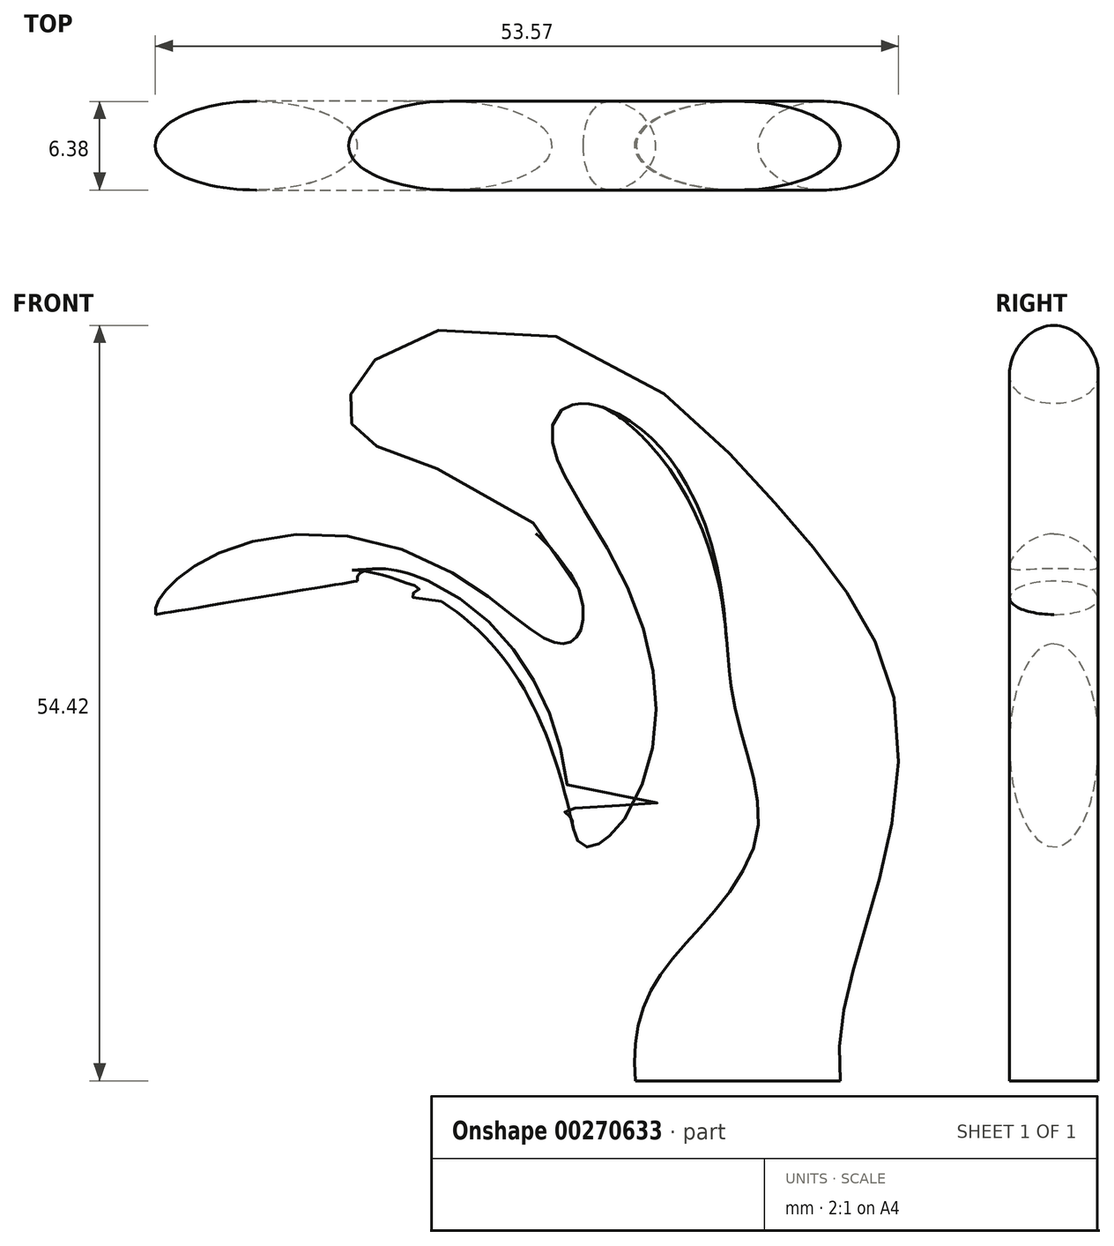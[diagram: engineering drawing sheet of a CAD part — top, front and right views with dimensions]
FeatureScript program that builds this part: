
annotation { "Feature Type Name" : "Feature", "Feature Type Description" : "" }
export const myFeature = defineFeature(function(context is Context, id is Id, definition is map)
    precondition{}
    {
        {
            var Q0;
            Q0=qCreatedBy(makeId("Top.planeOp"),FACE);
            var sketch = newSketch(context, id + "F0", { "sketchPlane" : qUnion([Q0])});
            skEllipse(sketch, "E0", {"center": v(0, 0) * mm, "majorRadius": 7.37 * mm, "minorRadius": 3.2 * mm, "majorAxis": v(1, 0)});
            skSolve(sketch);
        }
        {
            var Q0;
            Q0=qCreatedBy(makeId("Front.planeOp"),FACE);
            var sketch = newSketch(context, id + "F1", { "sketchPlane" : qUnion([Q0])});
            skLineSegment(sketch, "E1", {"start": v(0, 0) * mm, "end": v(0, 17.51) * mm});
            skFitSpline(sketch, "E2", {"points": [v(0, 17.51) * mm, v(-6, 33.73) * mm, v(-21.54, 36.47) * mm, v(-23.97, 24.31) * mm, v(-31.64, 21.07) * mm, v(-31.82, 17.51) * mm], "startDerivative": vector(-7.42, 72.24) * mm, "endDerivative": vector(9.9, -36.31) * mm});
            skSolve(sketch);
        }
        {
            var Q0;
            Q0=makeQuery(id+"F0.imprint","IMPRINT",FACE,{"disambiguationData":[TD([[makeQuery(id+"F0.imprint","IMPRINT",EDGE,{"derivedFrom":sQuery(id+"F0.wireOp",EDGE,"E0")}),1.0]])]});
            var Q1;
            Q1=sQuery(id+"F1.wireOp",EDGE,"E2");
            sweep(context, id + "F2", {"profiles" : qUnion([Q0]), "path" : qUnion([Q1])});
        }
    });
